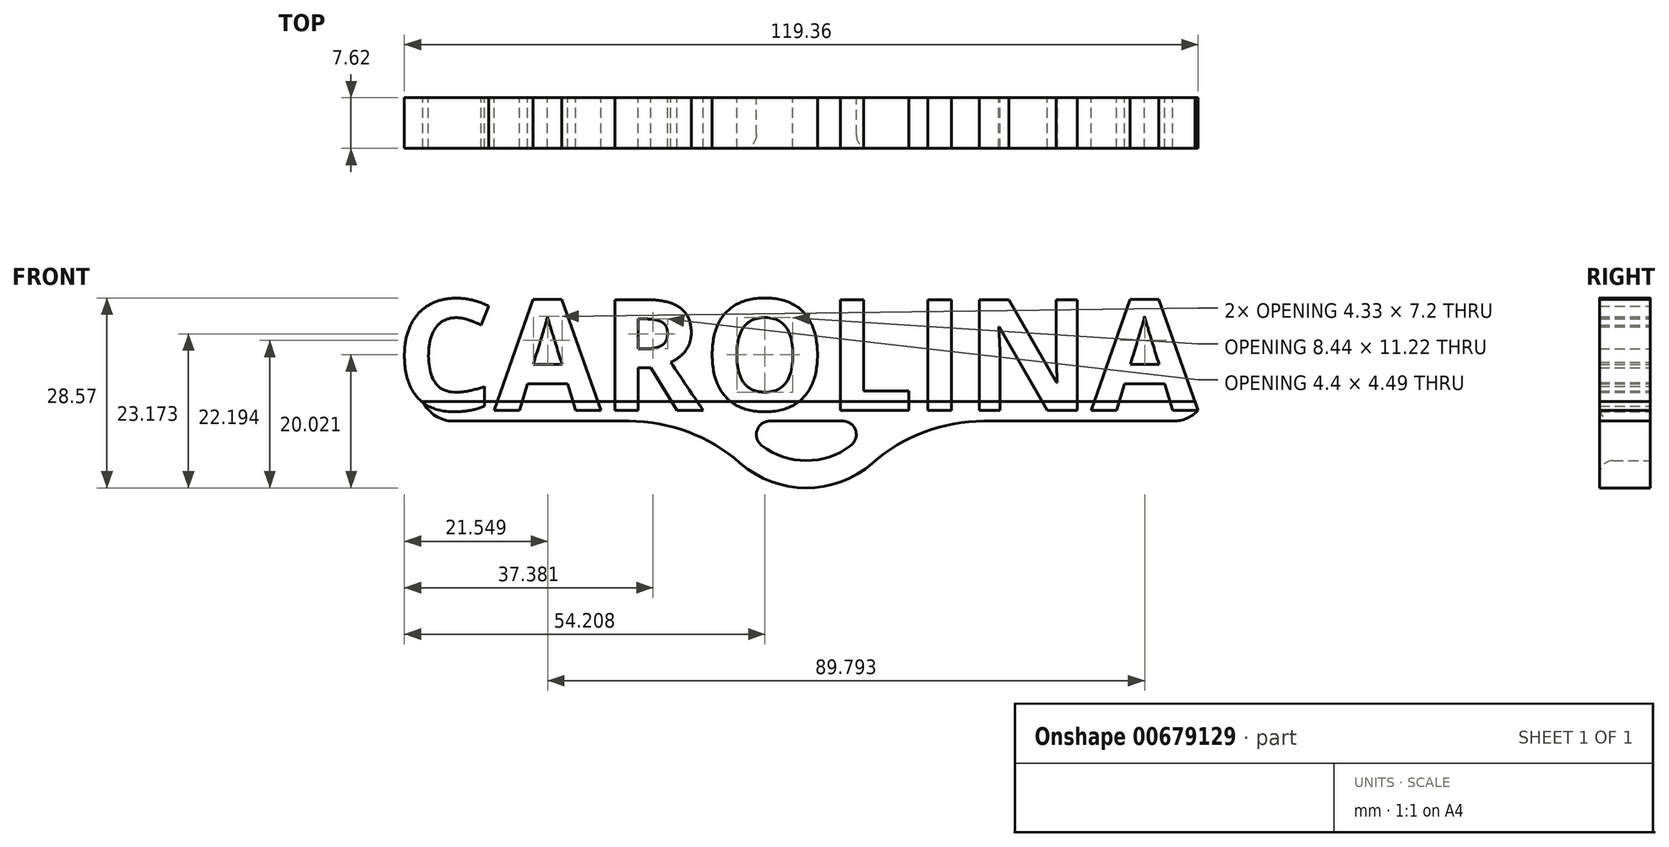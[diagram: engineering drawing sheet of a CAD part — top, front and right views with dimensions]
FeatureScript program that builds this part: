
annotation { "Feature Type Name" : "Feature", "Feature Type Description" : "" }
export const myFeature = defineFeature(function(context is Context, id is Id, definition is map)
    precondition{}
    {
        {
            var Q0;
            Q0=qCreatedBy(makeId("Front.planeOp"),FACE);
            var sketch = newSketch(context, id + "F0", { "sketchPlane" : qUnion([Q0])});
            skText(sketch, "E0", { "text": "CAROLINA", "fontName": "OpenSans-Bold.ttf"});
            const initialGuessF0  = {"E0": [-0.06033, 0, 1, 0, 0.01677]};
            skSetInitialGuess(sketch, initialGuessF0);
            skSolve(sketch);
        }
        {
            var Q0;
            Q0 = qSketchRegion(id + "F0", true);
            extrude(context, id + "F1", {"entities" : qUnion([Q0]), "depth" : 7.62 * mm, "offsetDistance" : 25.4 * mm});
        }
        {
            var Q0;
            Q0=qCreatedBy(makeId("Front.planeOp"),FACE);
            var sketch = newSketch(context, id + "F2", { "sketchPlane" : qUnion([Q0])});
            skLineSegment(sketch, "E1.bottom", {"start": v(59.93, 1.3) * mm, "end": v(-56.18, 1.3) * mm});
            skLineSegment(sketch, "E1.top", {"start": v(59.99, -1.63) * mm, "end": v(15.7, -1.63) * mm});
            skLineSegment(sketch, "E1.right", {"start": v(-56.18, 1.3) * mm, "end": v(-56.18, -1.63) * mm});
            skArc(sketch, "E2", {"start": v(-12.76, -1.63) * mm, "mid": v(1.47, -11.68) * mm, "end": v(15.7, -1.63) * mm});
            skArc(sketch, "E3.0", {"start": v(-8.29, -1.63) * mm, "mid": v(1.47, -7.57) * mm, "end": v(11.22, -1.63) * mm});
            skLineSegment(sketch, "E4.trimOffspring", {"start": v(-12.76, -1.63) * mm, "end": v(-56.18, -1.63) * mm});
            skLineSegment(sketch, "E5.trimOffspring", {"start": v(11.22, -1.63) * mm, "end": v(-8.29, -1.63) * mm});
            skLineSegment(sketch, "E6", {"start": v(59.99, -1.63) * mm, "end": v(60.38, 0) * mm});
            skLineSegment(sketch, "E7", {"start": v(59.93, 1.3) * mm, "end": v(60.38, 0) * mm});
            skSolve(sketch);
        }
        {
            var Q0;
            Q0 = qSketchRegion(id + "F2", true);
            extrude(context, id + "F3", {"entities" : qUnion([Q0]), "depth" : 7.62 * mm, "offsetDistance" : 25.4 * mm});
        }
        {
            var Q0;
            Q0=makeQuery(id+"F3.opExtrude","SWEPT_EDGE",EDGE,{"disambiguationData":[OSD([sQuery(id+"F2.wireOp",EDGE,"E1.top"),sQuery(id+"F2.wireOp",EDGE,"E2")])]});
            var Q1;
            Q1=makeQuery(id+"F3.opExtrude","SWEPT_EDGE",EDGE,{"disambiguationData":[OSD([sQuery(id+"F2.wireOp",EDGE,"E2"),sQuery(id+"F2.wireOp",EDGE,"E4.trimOffspring")])]});
            fillet(context, id + "F4", {"entities" : qUnion([Q0, Q1]), "radius" : 25.4 * mm, "tangentPropagation" : true, "allowEdgeOverflow" : false});
        }
        {
            var Q0;
            {var subQ0=sQuery(id+"F2.wireOp",EDGE,"E5.trimOffspring");var subQ1=sQuery(id+"F2.wireOp",EDGE,"E3.0");Q0=makeQuery(id+"F3.opExtrude","SWEPT_EDGE",EDGE,{"disambiguationData":[OSD([subQ1,subQ0]),TDD([makeQuery(id+"F2.imprint","INTERSECT",VERTEX,{"disambiguationData":[OD(1.0)],"derivedFrom":[subQ1,subQ0]})])]});}
            var Q1;
            {var subQ0=sQuery(id+"F2.wireOp",EDGE,"E5.trimOffspring");var subQ1=sQuery(id+"F2.wireOp",EDGE,"E3.0");Q1=makeQuery(id+"F3.opExtrude","SWEPT_EDGE",EDGE,{"disambiguationData":[OSD([subQ1,subQ0]),TDD([makeQuery(id+"F2.imprint","INTERSECT",VERTEX,{"disambiguationData":[OD(0.0)],"derivedFrom":[subQ1,subQ0]})])]});}
            fillet(context, id + "F5", {"entities" : qUnion([Q0, Q1]), "radius" : 2.03 * mm, "tangentPropagation" : true, "allowEdgeOverflow" : false});
        }
        {
            var Q0;
            Q0=makeQuery(id+"F3.opExtrude","SWEPT_EDGE",EDGE,{"disambiguationData":[OSD([sQuery(id+"F2.wireOp",EDGE,"E1.right"),sQuery(id+"F2.wireOp",EDGE,"E4.trimOffspring")])]});
            var Q1;
            Q1=makeQuery(id+"F3.opExtrude","SWEPT_EDGE",EDGE,{"disambiguationData":[OSD([sQuery(id+"F2.wireOp",EDGE,"E1.top"),sQuery(id+"F2.wireOp",EDGE,"E6")])]});
            fillet(context, id + "F6", {"entities" : qUnion([Q0, Q1]), "radius" : 5.08 * mm, "tangentPropagation" : true, "allowEdgeOverflow" : false});
        }
        {
            var Q0;
            Q0=makeQuery(id+"F3.opExtrude","CAP_EDGE",EDGE,{"disambiguationData":[OSD([sQuery(id+"F2.wireOp",EDGE,"E3.0")])],"isStart":false});
            fillet(context, id + "F7", {"entities" : qUnion([Q0]), "radius" : 2.03 * mm, "tangentPropagation" : true, "allowEdgeOverflow" : false});
        }
    });
